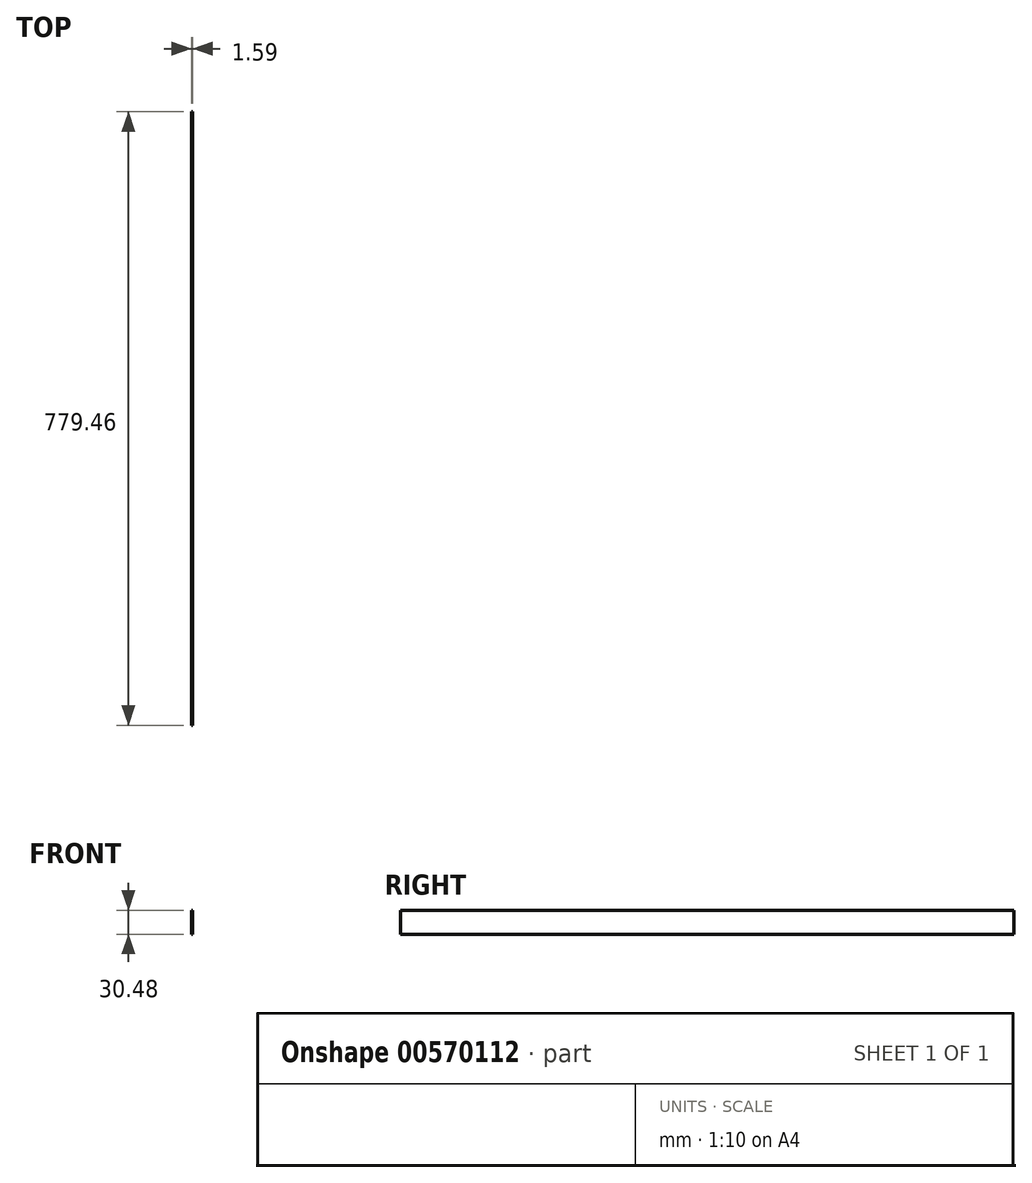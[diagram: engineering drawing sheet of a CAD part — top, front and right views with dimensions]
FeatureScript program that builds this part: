
annotation { "Feature Type Name" : "Feature", "Feature Type Description" : "" }
export const myFeature = defineFeature(function(context is Context, id is Id, definition is map)
    precondition{}
    {
        {
            var Q0;
            Q0=qCreatedBy(makeId("Front.planeOp"),FACE);
            var sketch = newSketch(context, id + "F0", { "sketchPlane" : qUnion([Q0])});
            skLineSegment(sketch, "E0.bottom", {"start": v(0, 0) * mm, "end": v(1.59, 0) * mm});
            skLineSegment(sketch, "E0.top", {"start": v(0, -30.48) * mm, "end": v(1.59, -30.48) * mm});
            skLineSegment(sketch, "E0.left", {"start": v(0, 0) * mm, "end": v(0, -30.48) * mm});
            skLineSegment(sketch, "E0.right", {"start": v(1.59, 0) * mm, "end": v(1.59, -30.48) * mm});
            skSolve(sketch);
        }
        {
            var Q0;
            Q0=makeQuery(id+"F0.imprint","IMPRINT",FACE,{"disambiguationData":[TD([[makeQuery(id+"F0.imprint","IMPRINT",EDGE,{"derivedFrom":sQuery(id+"F0.wireOp",EDGE,"E0.bottom")}),-1.0]])]});
            extrude(context, id + "F1", {"entities" : qUnion([Q0]), "depth" : 779.46 * mm, "offsetDistance" : 25.4 * mm});
        }
    });
